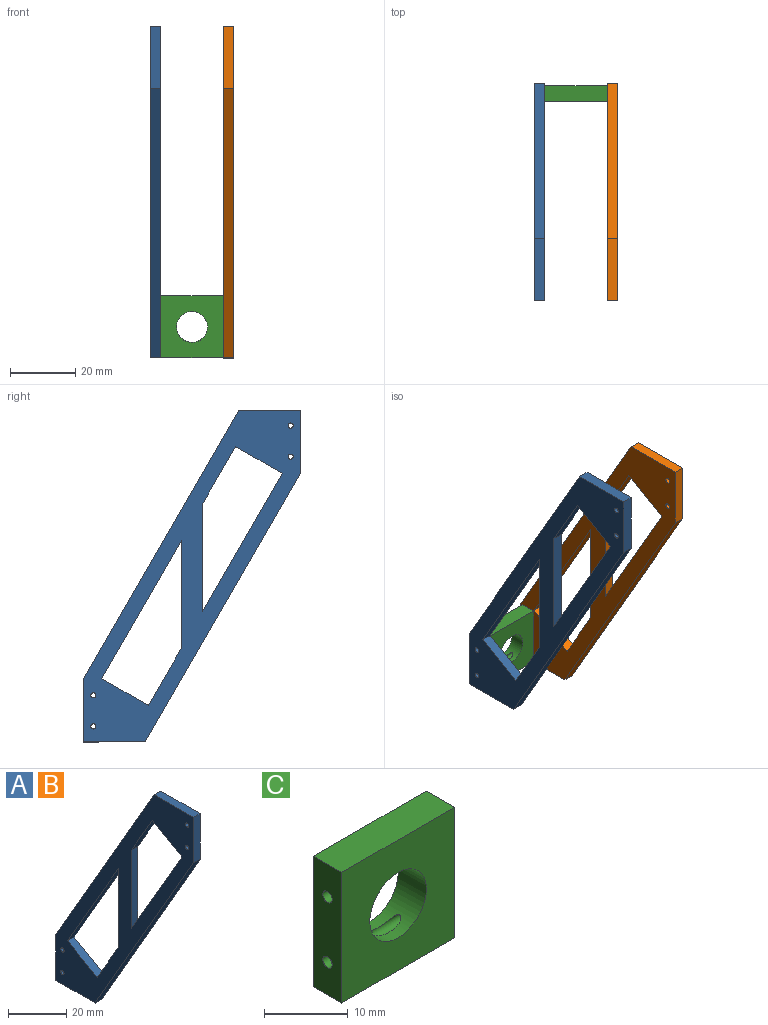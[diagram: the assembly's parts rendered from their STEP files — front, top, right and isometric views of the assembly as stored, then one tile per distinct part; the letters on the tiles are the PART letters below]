
ASSEMBLY  parts=3 mates=6
PART A: 20 faces, bbox 3.2x66.7x101.6 mm
  f0: plane 33x3.18mm, normal (0,-1,0), area 104.8mm2, adj f1,f17,f18,f19
  f1: plane 42.38x24.47mm, normal (0,0.87,0.5), area 155.4mm2, adj f0,f2,f18,f19
  f2: plane 14.29x8.25mm, normal (0,0.5,-0.87), area 52.4mm2, adj f1,f17,f18,f19
  f3: plane 82.55x47.66mm, normal (0,0.87,0.5), area 302.6mm2, adj f4,f11,f18,f19
  f4: plane 19.05x3.18mm, normal (0,0,1), area 60.5mm2, adj f3,f5,f18,f19
  f5: plane 19.05x3.18mm, normal (0,-1,0), area 60.5mm2, adj f4,f6,f18,f19
  f6: plane 82.55x47.66mm, normal (0,-0.87,-0.5), area 302.6mm2, adj f5,f7,f18,f19
  f7: plane 19.05x3.18mm, normal (0,0,-1), area 60.5mm2, adj f6,f11,f18,f19
  f8: plane 42.38x24.47mm, normal (0,-0.87,-0.5), area 155.4mm2, adj f9,f12,f18,f19
  f9: plane 14.29x8.25mm, normal (0,-0.5,0.87), area 52.4mm2, adj f8,f10,f18,f19
  f10: plane 17.63x10.18mm, normal (0,0.87,0.5), area 64.6mm2, adj f9,f12,f18,f19
  f11: plane 19.05x3.18mm, normal (0,1,0), area 60.5mm2, adj f3,f7,f18,f19
  f12: plane 33x3.18mm, normal (0,1,0), area 104.8mm2, adj f8,f10,f18,f19
  f13: cylinder r=0.79mm len=3.18mm, axis (-1,0,0), area 15.8mm2, adj f18,f19
  f14: cylinder r=0.79mm len=3.18mm, axis (-1,0,0), area 15.8mm2, adj f18,f19
  f15: cylinder r=0.79mm len=3.18mm, axis (-1,0,0), area 15.8mm2, adj f18,f19
  f16: cylinder r=0.79mm len=3.18mm, axis (-1,0,0), area 15.8mm2, adj f18,f19
  f17: plane 17.63x10.18mm, normal (0,-0.87,-0.5), area 64.6mm2, adj f0,f2,f18,f19
  f18: plane 101.6x66.71mm, normal (1,0,0), area 1692.2mm2, adj f0,f1,f2,f3,f4,f5,f6,f7
  f19: plane 101.6x66.71mm, normal (-1,0,0), area 1692.2mm2, adj f0,f1,f2,f3,f4,f5,f6,f7
PART B: same geometry as A
PART C: 9 faces, bbox 19.1x4.8x19.1 mm
  f0: plane 19.05x19.05mm, normal (0,-1,0), area 291.6mm2, adj f1,f5,f6,f7,f8
  f1: plane 19.05x4.76mm, normal (0,0,-1), area 90.7mm2, adj f0,f2,f6,f7
  f2: plane 19.05x19.05mm, normal (0,1,0), area 291.6mm2, adj f1,f5,f6,f7,f8
  f3: cylinder r=0.79mm len=19.05mm, axis (-1,0,0), area 84.9mm2, adj f6,f7,f8
  f4: cylinder r=0.79mm len=19.05mm, axis (-1,0,0), area 84.9mm2, adj f6,f7,f8
  f5: plane 19.05x4.76mm, normal (0,0,1), area 90.7mm2, adj f0,f2,f6,f7
  f6: plane 19.05x4.76mm, normal (1,0,0), area 86.8mm2, adj f0,f1,f2,f3,f4,f5
  f7: plane 19.05x4.76mm, normal (-1,0,0), area 86.8mm2, adj f0,f1,f2,f3,f4,f5
  f8: cylinder r=4.76mm len=9.53mm, axis (0,1,0), area 127.2mm2, adj f0,f2,f3,f4
PLACE A t=(-20.73,-23.74,35.27)mm
PLACE B t=(1.5,-23.74,35.27)mm
PLACE C t=(-17.55,39.79,-56.81)mm
MATE planar C.f7 <-> A.f18  axis (-1,0,0) through (-17.55,37.41,-56.81)mm
MATE planar C.f6 <-> B.f19  axis (1,0,0) through (1.5,39.79,-56.81)mm
MATE cylindrical C.f3 <-> A.f15  axis (-1,0,0) through (-8.03,39.79,-52.04)mm
MATE cylindrical C.f4 <-> B.f16  axis (1,0,0) through (1.5,39.79,-61.57)mm
MATE cylindrical B.f16 <-> A.f16  axis (-1,0,0) through (1.5,39.79,-61.57)mm
MATE cylindrical B.f13 <-> A.f13  axis (-1,0,0) through (1.5,-20.57,30.51)mm
